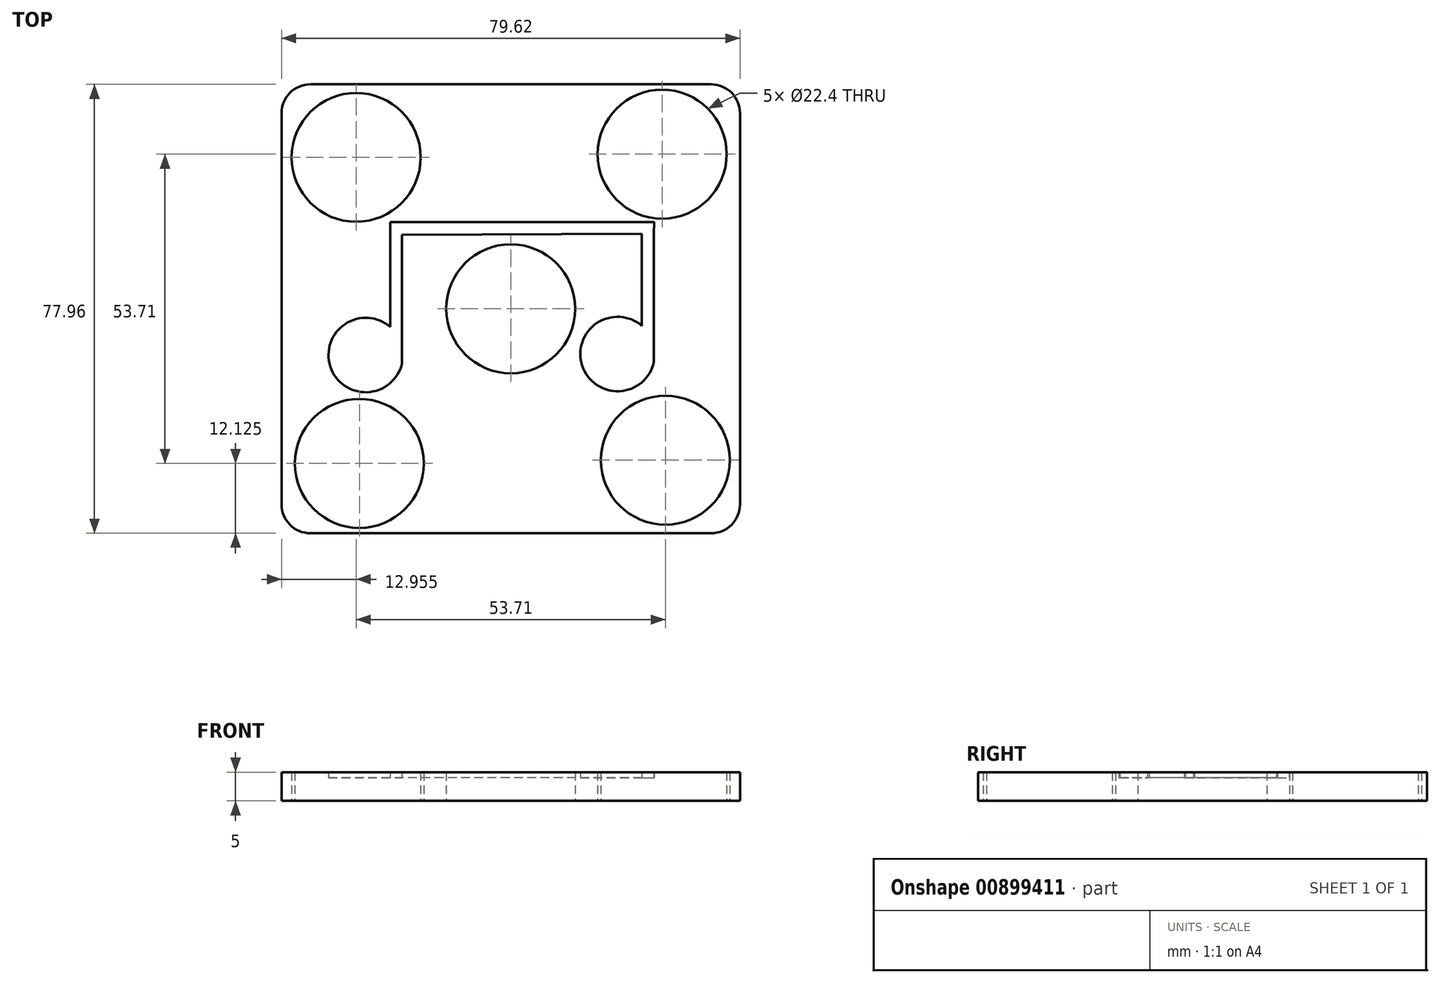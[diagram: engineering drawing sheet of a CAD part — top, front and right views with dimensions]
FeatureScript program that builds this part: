
annotation { "Feature Type Name" : "Feature", "Feature Type Description" : "" }
export const myFeature = defineFeature(function(context is Context, id is Id, definition is map)
    precondition{}
    {
        {
            var Q0;
            Q0=qCreatedBy(makeId("Top.planeOp"),FACE);
            var sketch = newSketch(context, id + "F0", { "sketchPlane" : qUnion([Q0])});
            skPoint(sketch, "E0.middle", {"position": v(0, 0) * mm});
            skCircle(sketch, "E1", {"center": v(0, 0) * mm, "radius": 11.2 * mm});
            skCircle(sketch, "E2", {"center": v(-26.3, -26.85) * mm, "radius": 11.2 * mm});
            skCircle(sketch, "E3.1.0", {"center": v(26.85, -26.3) * mm, "radius": 11.2 * mm});
            skCircle(sketch, "E3.2.0", {"center": v(26.3, 26.85) * mm, "radius": 11.2 * mm});
            skCircle(sketch, "E3.3.0", {"center": v(-26.85, 26.3) * mm, "radius": 11.2 * mm});
            skLineSegment(sketch, "E4.bottom", {"start": v(22.77, 13.05) * mm, "end": v(-18.91, 12.86) * mm});
            skLineSegment(sketch, "E4.top", {"start": v(22.8, 15.07) * mm, "end": v(-20.96, 15.07) * mm});
            skLineSegment(sketch, "E4.left", {"start": v(24.87, 13.05) * mm, "end": v(24.9, 15.07) * mm});
            skLineSegment(sketch, "E4.right", {"start": v(-20.96, 12.85) * mm, "end": v(-20.96, 15.07) * mm});
            skLineSegment(sketch, "E5", {"start": v(-20.96, 12.85) * mm, "end": v(-20.96, -3.15) * mm});
            skLineSegment(sketch, "E6", {"start": v(-18.9, 12.23) * mm, "end": v(-18.9, -6.51) * mm});
            skArc(sketch, "E7", {"start": v(-20.96, -3.15) * mm, "mid": v(-31.36, -10) * mm, "end": v(-18.9, -9.55) * mm});
            skLineSegment(sketch, "E8", {"start": v(-18.9, -6.51) * mm, "end": v(-18.9, -9.55) * mm});
            skLineSegment(sketch, "E9", {"start": v(24.87, 13.05) * mm, "end": v(24.87, -9.26) * mm});
            skLineSegment(sketch, "E10", {"start": v(22.77, 13.05) * mm, "end": v(22.77, -2.95) * mm});
            skArc(sketch, "E11", {"start": v(22.77, -2.95) * mm, "mid": v(12.42, -9.9) * mm, "end": v(24.87, -9.26) * mm});
            skLineSegment(sketch, "E12", {"start": v(-18.9, 12.23) * mm, "end": v(-18.91, 12.86) * mm});
            skLineSegment(sketch, "E13", {"start": v(22.8, 15.07) * mm, "end": v(24.9, 15.07) * mm});
            skLineSegment(sketch, "E14.bottom", {"start": v(34.8, 38.98) * mm, "end": v(-34.8, 38.98) * mm});
            skLineSegment(sketch, "E14.top", {"start": v(34.8, -38.98) * mm, "end": v(-34.8, -38.98) * mm});
            skLineSegment(sketch, "E14.left", {"start": v(39.8, 33.98) * mm, "end": v(39.8, -33.98) * mm});
            skLineSegment(sketch, "E14.right", {"start": v(-39.8, 33.98) * mm, "end": v(-39.8, -33.98) * mm});
            skPoint(sketch, "E15.visualSharp", {"position": v(-39.8, 38.98) * mm});
            skArc(sketch, "E15.filletArc", {"start": v(-34.8, 38.98) * mm, "mid": v(-38.35, 37.51) * mm, "end": v(-39.8, 33.98) * mm});
            skPoint(sketch, "E16.visualSharp", {"position": v(39.8, 38.98) * mm});
            skArc(sketch, "E16.filletArc", {"start": v(39.8, 33.98) * mm, "mid": v(38.35, 37.51) * mm, "end": v(34.8, 38.98) * mm});
            skPoint(sketch, "E17.visualSharp", {"position": v(39.8, -38.98) * mm});
            skArc(sketch, "E17.filletArc", {"start": v(34.8, -38.98) * mm, "mid": v(38.35, -37.51) * mm, "end": v(39.8, -33.98) * mm});
            skPoint(sketch, "E18.visualSharp", {"position": v(-39.8, -38.98) * mm});
            skArc(sketch, "E18.filletArc", {"start": v(-39.8, -33.98) * mm, "mid": v(-38.35, -37.51) * mm, "end": v(-34.8, -38.98) * mm});
            skSolve(sketch);
        }
        {
            var Q0;
            Q0=makeQuery(id+"F0.imprint","IMPRINT",FACE,{"disambiguationData":[TD([[makeQuery(id+"F0.imprint","IMPRINT",EDGE,{"derivedFrom":sQuery(id+"F0.wireOp",EDGE,"E1")}),-1.0]])]});
            extrude(context, id + "F1", {"entities" : qUnion([Q0]), "depth" : 5 * mm, "offsetDistance" : 25 * mm});
        }
        {
            var Q0;
            Q0=makeQuery(id+"F0.imprint","IMPRINT",FACE,{"disambiguationData":[TD([[makeQuery(id+"F0.imprint","IMPRINT",EDGE,{"derivedFrom":sQuery(id+"F0.wireOp",EDGE,"E4.bottom")}),-1.0]])]});
            extrude(context, id + "F2", {"entities" : qUnion([Q0]), "operationType" : NewBodyOperationType.ADD, "depth" : 4 * mm, "offsetDistance" : 25 * mm});
        }
    });
